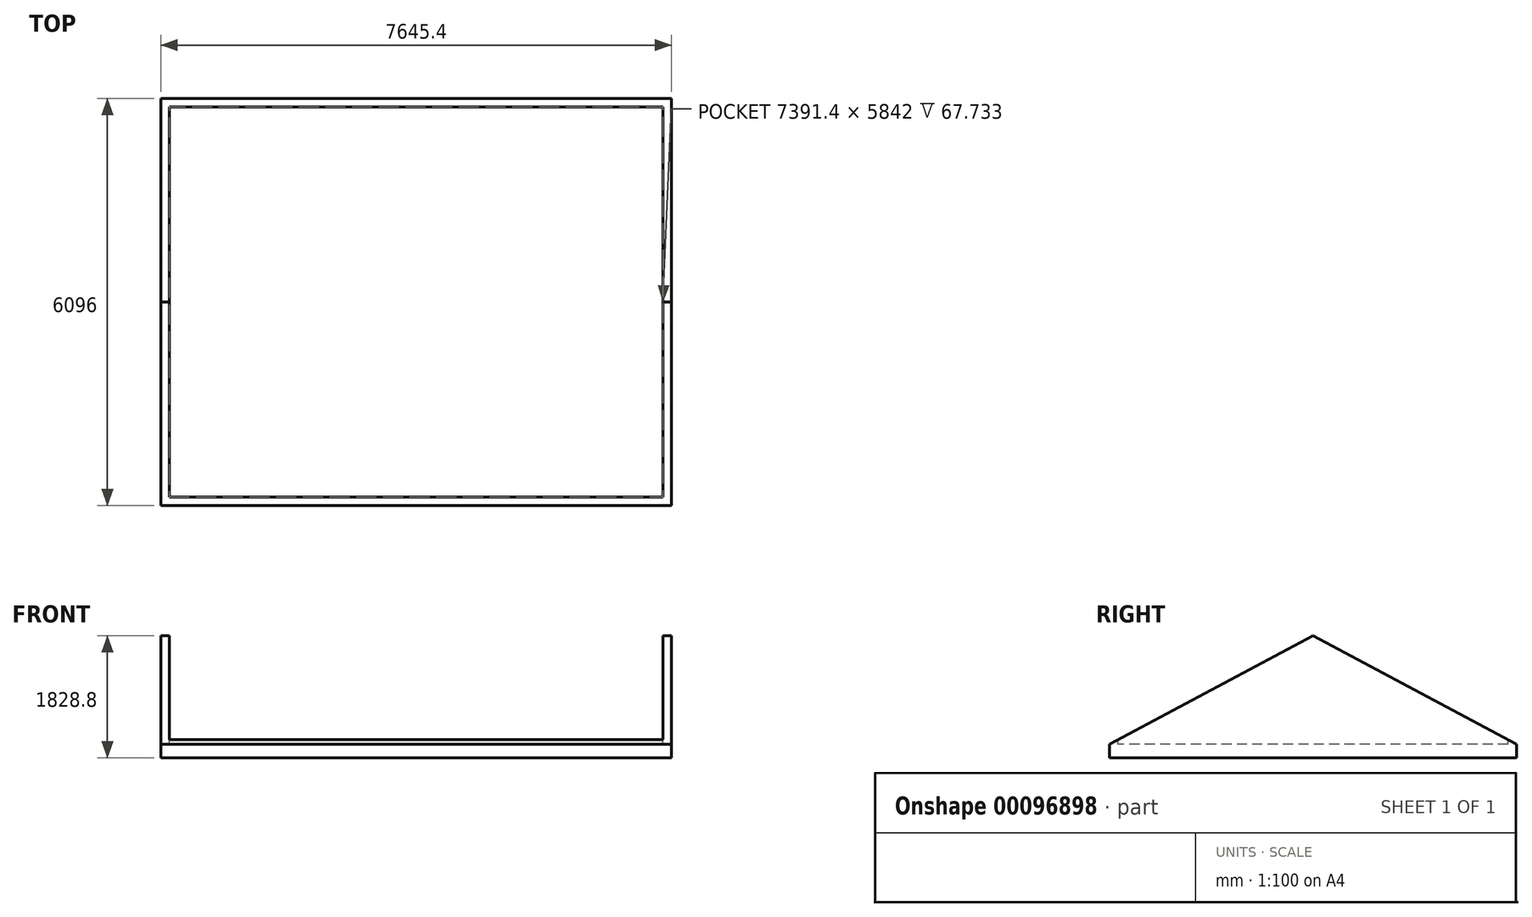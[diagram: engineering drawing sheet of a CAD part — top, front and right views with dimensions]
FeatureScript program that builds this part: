
annotation { "Feature Type Name" : "Feature", "Feature Type Description" : "" }
export const myFeature = defineFeature(function(context is Context, id is Id, definition is map)
    precondition{}
    {
        {
            var Q0;
            Q0=qCreatedBy(makeId("Top.planeOp"),FACE);
            cPlane(context, id + "F0", {"entities" : qUnion([Q0]), "cplaneType" : CPlaneType.OFFSET, "offset" : 1828.8 * mm, "width" : 152.4 * mm, "height" : 152.4 * mm});
        }
        {
            var Q0;
            Q0=qCreatedBy(makeId("Right.planeOp"),FACE);
            var sketch = newSketch(context, id + "F1", { "sketchPlane" : qUnion([Q0])});
            skLineSegment(sketch, "E0", {"start": v(0, 0) * mm, "end": v(6096, 0) * mm});
            skLineSegment(sketch, "E1", {"start": v(6096, 0) * mm, "end": v(6096, 203.2) * mm});
            skLineSegment(sketch, "E2", {"start": v(3048, 0) * mm, "end": v(3048, 1828.8) * mm, "construction": true});
            skLineSegment(sketch, "E3", {"start": v(3048, 1828.8) * mm, "end": v(6096, 203.2) * mm});
            skLineSegment(sketch, "E4.MirrorCS", {"start": v(3048, 1828.8) * mm, "end": v(0, 203.2) * mm});
            skLineSegment(sketch, "E5.MirrorCS", {"start": v(0, 0) * mm, "end": v(0, 203.2) * mm});
            skSolve(sketch);
        }
        {
            var Q0;
            Q0 = qSketchRegion(id + "F1", true);
            extrude(context, id + "F2", {"entities" : qUnion([Q0]), "depth" : 7645.4 * mm});
        }
        {
            var Q0;
            Q0=qCreatedBy(id+"F0.planeOp",FACE);
            var sketch = newSketch(context, id + "F3", { "sketchPlane" : qUnion([Q0])});
            skLineSegment(sketch, "E6.bottom", {"start": v(127, 5969) * mm, "end": v(7518.4, 5969) * mm});
            skLineSegment(sketch, "E6.top", {"start": v(127, 127) * mm, "end": v(7518.4, 127) * mm});
            skLineSegment(sketch, "E6.left", {"start": v(127, 5969) * mm, "end": v(127, 127) * mm});
            skLineSegment(sketch, "E6.right", {"start": v(7518.4, 5969) * mm, "end": v(7518.4, 127) * mm});
            skSolve(sketch);
        }
        {
            var Q0;
            Q0 = qSketchRegion(id + "F3", true);
            extrude(context, id + "F4", {"entities" : qUnion([Q0]), "operationType" : NewBodyOperationType.REMOVE, "oppositeDirection" : true, "depth" : 1625.6 * mm});
        }
    });
